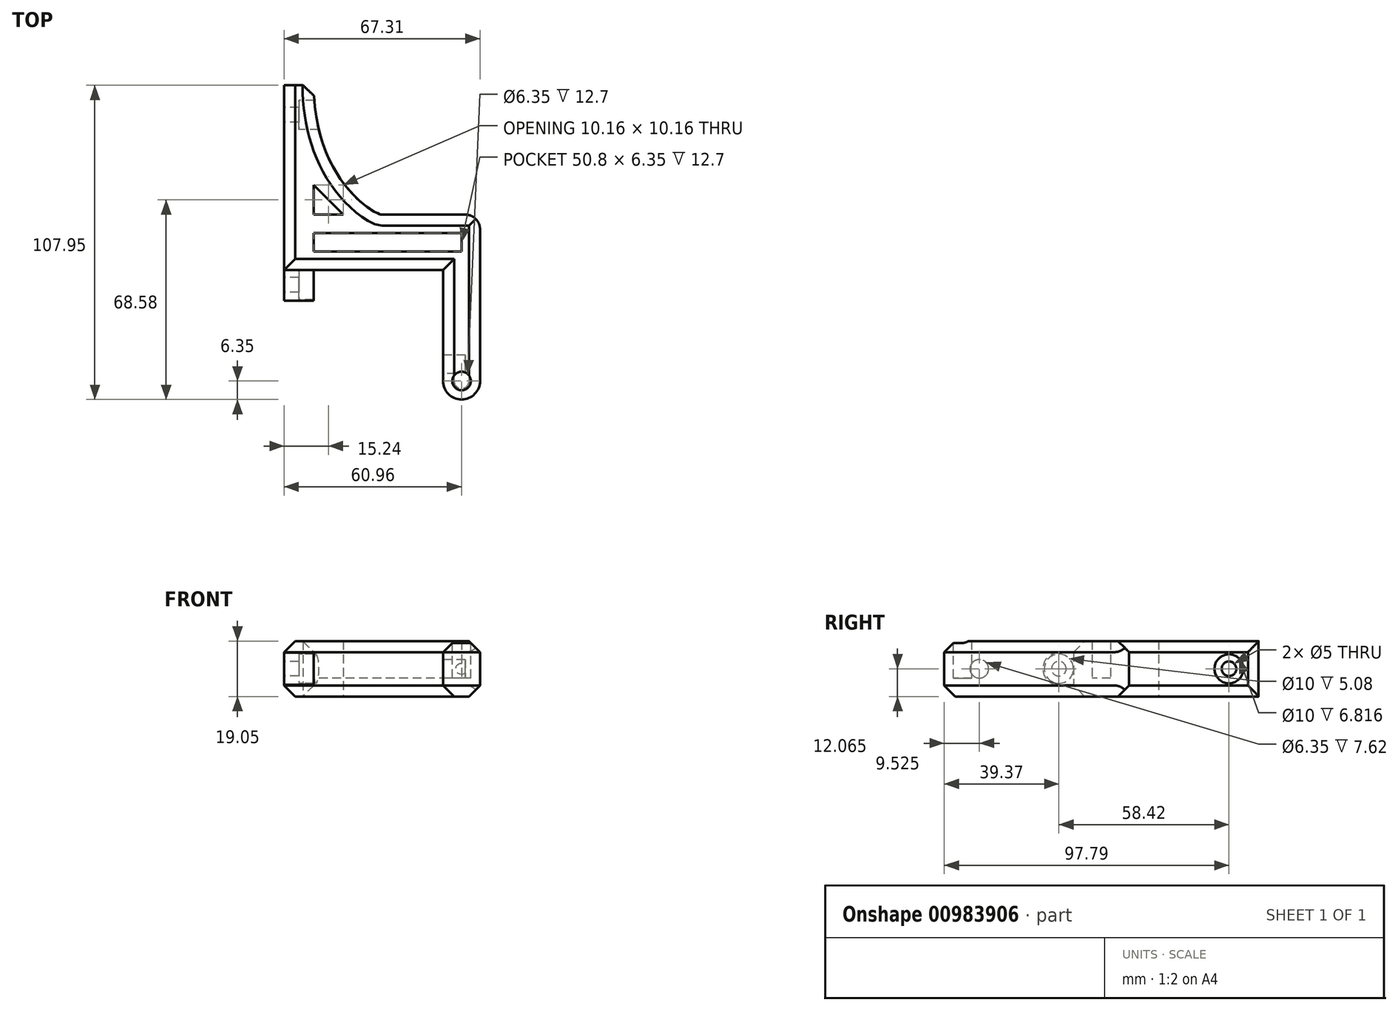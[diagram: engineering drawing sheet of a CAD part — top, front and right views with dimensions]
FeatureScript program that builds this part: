
annotation { "Feature Type Name" : "Feature", "Feature Type Description" : "" }
export const myFeature = defineFeature(function(context is Context, id is Id, definition is map)
    precondition{}
    {
        {
            var Q0;
            Q0=qCreatedBy(makeId("Top.planeOp"),FACE);
            var sketch = newSketch(context, id + "F0", { "sketchPlane" : qUnion([Q0])});
            skLineSegment(sketch, "E0", {"start": v(0, 0) * mm, "end": v(0, 63.5) * mm});
            skLineSegment(sketch, "E1", {"start": v(0, 63.5) * mm, "end": v(10.16, 63.5) * mm});
            skLineSegment(sketch, "E2", {"start": v(0, 0) * mm, "end": v(67.3, 0) * mm});
            skLineSegment(sketch, "E3", {"start": v(67.3, 0) * mm, "end": v(67.3, 19.05) * mm});
            skLineSegment(sketch, "E4", {"start": v(67.3, 19.05) * mm, "end": v(33.65, 19.05) * mm});
            skLineSegment(sketch, "E5", {"start": v(10.16, 19.05) * mm, "end": v(10.16, 29.21) * mm});
            skLineSegment(sketch, "E6", {"start": v(10.16, 29.21) * mm, "end": v(20.32, 19.05) * mm});
            skLineSegment(sketch, "E7", {"start": v(20.32, 19.05) * mm, "end": v(10.16, 19.05) * mm});
            skLineSegment(sketch, "E8", {"start": v(33.65, 63.55) * mm, "end": v(33.65, 0) * mm, "construction": true});
            skPoint(sketch, "E9.positionSnap0", {"position": v(67.3, 9.53) * mm});
            skLineSegment(sketch, "E10.bottom", {"start": v(60.96, 12.7) * mm, "end": v(10.16, 12.7) * mm});
            skLineSegment(sketch, "E10.top", {"start": v(60.96, 6.35) * mm, "end": v(10.16, 6.35) * mm});
            skLineSegment(sketch, "E10.left", {"start": v(60.96, 12.7) * mm, "end": v(60.96, 6.35) * mm});
            skLineSegment(sketch, "E10.right", {"start": v(10.16, 12.7) * mm, "end": v(10.16, 6.35) * mm});
            skPoint(sketch, "E10.middle", {"position": v(33.65, 9.53) * mm});
            skFitSpline(sketch, "E11", {"points": [v(10.16, 63.5) * mm, v(33.65, 19.05) * mm], "startDerivative": vector(0, -95.25) * mm, "endDerivative": vector(8.92, 0) * mm});
            skPoint(sketch, "E12", {"position": v(0, 31.75) * mm});
            skLineSegment(sketch, "E13", {"start": v(67.3, 0) * mm, "end": v(67.3, -38.1) * mm});
            skLineSegment(sketch, "E14", {"start": v(54.6, 0) * mm, "end": v(54.6, -38.1) * mm});
            skArc(sketch, "E15", {"start": v(54.6, -38.1) * mm, "mid": v(60.96, -44.45) * mm, "end": v(67.3, -38.1) * mm});
            skSolve(sketch);
        }
        {
            var Q0;
            {var subQ1=sQuery(id+"F0.wireOp",EDGE,"E0");Q0=makeQuery(id+"F0.imprint","IMPRINT",FACE,{"disambiguationData":[TD([[makeQuery(id+"F0.imprint","IMPRINT",EDGE,{"derivedFrom":subQ1}),-1.0]])]});}
            var Q1;
            {var subQ0=sQuery(id+"F0.wireOp",EDGE,"E13");Q1=makeQuery(id+"F0.imprint","IMPRINT",FACE,{"disambiguationData":[TD([[makeQuery(id+"F0.imprint","IMPRINT",EDGE,{"derivedFrom":subQ0}),-1.0]])]});}
            extrude(context, id + "F1", {"entities" : qUnion([Q0, Q1]), "depth" : 19.05 * mm, "offsetDistance" : 25.4 * mm});
        }
        {
            var Q0;
            Q0=makeQuery(id+"F0.imprint","IMPRINT",FACE,{"disambiguationData":[TD([[makeQuery(id+"F0.imprint","IMPRINT",EDGE,{"derivedFrom":sQuery(id+"F0.wireOp",EDGE,"E10.bottom")}),1.0]])]});
            extrude(context, id + "F2", {"entities" : qUnion([Q0]), "operationType" : NewBodyOperationType.ADD, "depth" : 6.35 * mm, "offsetDistance" : 25.4 * mm});
        }
        {
            var Q0;
            Q0=makeQuery(id+"F1.opExtrude","CAP_FACE",FACE,{"disambiguationData":[OSD([sQuery(id+"F0.wireOp",EDGE,"E0"),sQuery(id+"F0.wireOp",EDGE,"E1"),sQuery(id+"F0.wireOp",EDGE,"E2"),sQuery(id+"F0.wireOp",EDGE,"E3"),sQuery(id+"F0.wireOp",EDGE,"E4"),sQuery(id+"F0.wireOp",EDGE,"E5"),sQuery(id+"F0.wireOp",EDGE,"E6"),sQuery(id+"F0.wireOp",EDGE,"E7"),sQuery(id+"F0.wireOp",EDGE,"E10.bottom"),sQuery(id+"F0.wireOp",EDGE,"E10.top"),sQuery(id+"F0.wireOp",EDGE,"E10.left"),sQuery(id+"F0.wireOp",EDGE,"E10.right"),sQuery(id+"F0.wireOp",EDGE,"E11"),sQuery(id+"F0.wireOp",EDGE,"E13"),sQuery(id+"F0.wireOp",EDGE,"E14"),sQuery(id+"F0.wireOp",EDGE,"E15")])],"isStart":false});
            var sketch = newSketch(context, id + "F3", { "sketchPlane" : qUnion([Q0])});
            skCircle(sketch, "E16", {"center": v(60.96, -38.1) * mm, "radius": 3.18 * mm});
            skSolve(sketch);
        }
        {
            var Q0;
            Q0=makeQuery(id+"F3.imprint","IMPRINT",FACE,{"disambiguationData":[TD([[makeQuery(id+"F3.imprint","IMPRINT",EDGE,{"derivedFrom":sQuery(id+"F3.wireOp",EDGE,"E16")}),1.0]])]});
            extrude(context, id + "F4", {"entities" : qUnion([Q0]), "operationType" : NewBodyOperationType.REMOVE, "oppositeDirection" : true, "depth" : 12.7 * mm, "offsetDistance" : 25.4 * mm});
        }
        {
            var Q0;
            Q0=makeQuery(id+"F1.opExtrude","SWEPT_FACE",FACE,{"disambiguationData":[OSD([sQuery(id+"F0.wireOp",EDGE,"E0")])]});
            var sketch = newSketch(context, id + "F5", { "sketchPlane" : qUnion([Q0])});
            skLineSegment(sketch, "E17", {"start": v(-3.18, 9.53) * mm, "end": v(0, 9.53) * mm, "construction": true});
            skLineSegment(sketch, "E18", {"start": v(0, 15.03) * mm, "end": v(5.08, 15.03) * mm});
            skLineSegment(sketch, "E19.MirrorCS", {"start": v(0, 4.03) * mm, "end": v(5.08, 4.03) * mm});
            skArc(sketch, "E20", {"start": v(5.08, 4.03) * mm, "mid": v(10.58, 9.53) * mm, "end": v(5.08, 15.03) * mm});
            skCircle(sketch, "E21", {"center": v(5.08, 9.53) * mm, "radius": 5 * mm});
            skCircle(sketch, "E22", {"center": v(-53.34, 9.53) * mm, "radius": 5 * mm});
            skPoint(sketch, "E22.centerSnap0", {"position": v(-63.5, 9.53) * mm});
            skCircle(sketch, "E23", {"center": v(-53.34, 9.53) * mm, "radius": 2.5 * mm});
            skCircle(sketch, "E24", {"center": v(5.08, 9.53) * mm, "radius": 2.5 * mm});
            skSolve(sketch);
        }
        {
            var Q0;
            {var subQ1=sQuery(id+"F5.wireOp",EDGE,"E18");Q0=makeQuery(id+"F5.imprint","IMPRINT",FACE,{"disambiguationData":[TD([[makeQuery(id+"F5.imprint","IMPRINT",EDGE,{"derivedFrom":subQ1}),-1.0]])]});}
            extrude(context, id + "F6", {"entities" : qUnion([Q0]), "operationType" : NewBodyOperationType.ADD, "oppositeDirection" : true, "depth" : 10.16 * mm, "offsetDistance" : 25.4 * mm});
        }
        {
            var Q0;
            Q0=makeQuery(id+"F5.imprint","IMPRINT",FACE,{"disambiguationData":[TD([[makeQuery(id+"F5.imprint","IMPRINT",EDGE,{"derivedFrom":sQuery(id+"F5.wireOp",EDGE,"E21")}),1.0]])]});
            extrude(context, id + "F7", {"entities" : qUnion([Q0]), "operationType" : NewBodyOperationType.ADD, "oppositeDirection" : true, "depth" : 5.08 * mm, "offsetDistance" : 25.4 * mm});
        }
        {
            var Q0;
            Q0=makeQuery(id+"F5.imprint","IMPRINT",FACE,{"disambiguationData":[TD([[makeQuery(id+"F5.imprint","IMPRINT",EDGE,{"derivedFrom":sQuery(id+"F5.wireOp",EDGE,"E23")}),1.0]])]});
            extrude(context, id + "F8", {"entities" : qUnion([Q0]), "operationType" : NewBodyOperationType.REMOVE, "endBound" : BoundingType.THROUGH_ALL, "oppositeDirection" : true, "depth" : 25.4 * mm, "offsetDistance" : 25.4 * mm});
        }
        {
            var Q0;
            Q0=makeQuery(id+"F5.imprint","IMPRINT",FACE,{"disambiguationData":[TD([[makeQuery(id+"F5.imprint","IMPRINT",EDGE,{"derivedFrom":sQuery(id+"F5.wireOp",EDGE,"E22")}),1.0]])]});
            extrude(context, id + "F9", {"entities" : qUnion([Q0]), "operationType" : NewBodyOperationType.REMOVE, "endBound" : BoundingType.THROUGH_ALL, "oppositeDirection" : true, "depth" : 25.4 * mm, "offsetDistance" : 25.4 * mm, "hasSecondDirection" : true, "secondDirectionOppositeDirection" : true, "secondDirectionDepth" : 5.08 * mm});
        }
        {
            var Q0;
            Q0=makeQuery(id+"F1.opExtrude","CAP_EDGE",EDGE,{"disambiguationData":[OSD([sQuery(id+"F0.wireOp",EDGE,"E3"),sQuery(id+"F0.wireOp",EDGE,"E13")])],"isStart":false});
            var Q1;
            Q1=makeQuery(id+"F1.opExtrude","CAP_EDGE",EDGE,{"disambiguationData":[OSD([sQuery(id+"F0.wireOp",EDGE,"E2")])],"isStart":false});
            var Q2;
            Q2=makeQuery(id+"F1.opExtrude","CAP_EDGE",EDGE,{"disambiguationData":[OSD([sQuery(id+"F0.wireOp",EDGE,"E0")])],"isStart":false});
            var Q3;
            Q3=makeQuery(id+"F1.opExtrude","CAP_EDGE",EDGE,{"disambiguationData":[OSD([sQuery(id+"F0.wireOp",EDGE,"E4")])],"isStart":false});
            var Q4;
            Q4=makeQuery(id+"F1.opExtrude","SWEPT_EDGE",EDGE,{"disambiguationData":[OSD([sQuery(id+"F0.wireOp",EDGE,"E1"),sQuery(id+"F0.wireOp",EDGE,"E11")])]});
            var Q5;
            Q5=makeQuery(id+"F1.opExtrude","CAP_EDGE",EDGE,{"disambiguationData":[OSD([sQuery(id+"F0.wireOp",EDGE,"E2")])],"isStart":true});
            var Q6;
            Q6=makeQuery(id+"F1.opExtrude","CAP_EDGE",EDGE,{"disambiguationData":[OSD([sQuery(id+"F0.wireOp",EDGE,"E14")])],"isStart":true});
            var Q7;
            Q7=makeQuery(id+"F1.opExtrude","CAP_EDGE",EDGE,{"disambiguationData":[OSD([sQuery(id+"F0.wireOp",EDGE,"E4")])],"isStart":true});
            var Q8;
            Q8=makeQuery(id+"F1.opExtrude","CAP_EDGE",EDGE,{"disambiguationData":[OSD([sQuery(id+"F0.wireOp",EDGE,"E0")])],"isStart":true});
            chamfer(context, id + "F10", {"entities" : qUnion([Q0, Q1, Q2, Q3, Q4, Q5, Q6, Q7, Q8]), "chamferType" : ChamferType.OFFSET_ANGLE, "width" : 3.8 * mm, "oppositeDirection" : false, "angle" : 45 * degree, "tangentPropagation" : true});
        }
        {
            var Q0;
            Q0=makeQuery(id+"F1.opExtrude","SWEPT_EDGE",EDGE,{"disambiguationData":[OSD([sQuery(id+"F0.wireOp",EDGE,"E3"),sQuery(id+"F0.wireOp",EDGE,"E4")])]});
            fillet(context, id + "F11", {"entities" : qUnion([Q0]), "radius" : 5.08 * mm, "tangentPropagation" : true, "allowEdgeOverflow" : false});
        }
        {
            var Q0;
            Q0=makeQuery(id+"F1.opExtrude","SWEPT_FACE",FACE,{"disambiguationData":[OSD([sQuery(id+"F0.wireOp",EDGE,"E14")])]});
            var sketch = newSketch(context, id + "F12", { "sketchPlane" : qUnion([Q0])});
            skCircle(sketch, "E25", {"center": v(32.38, 9.53) * mm, "radius": 3.18 * mm});
            skPoint(sketch, "E25.centerSnap0", {"position": v(38.1, 9.53) * mm});
            skSolve(sketch);
        }
        {
            var Q0;
            Q0=makeQuery(id+"F12.imprint","IMPRINT",FACE,{"disambiguationData":[TD([[makeQuery(id+"F12.imprint","IMPRINT",EDGE,{"derivedFrom":sQuery(id+"F12.wireOp",EDGE,"E25")}),1.0]])]});
            extrude(context, id + "F13", {"entities" : qUnion([Q0]), "operationType" : NewBodyOperationType.REMOVE, "oppositeDirection" : true, "depth" : 7.62 * mm, "offsetDistance" : 25.4 * mm});
        }
    });
